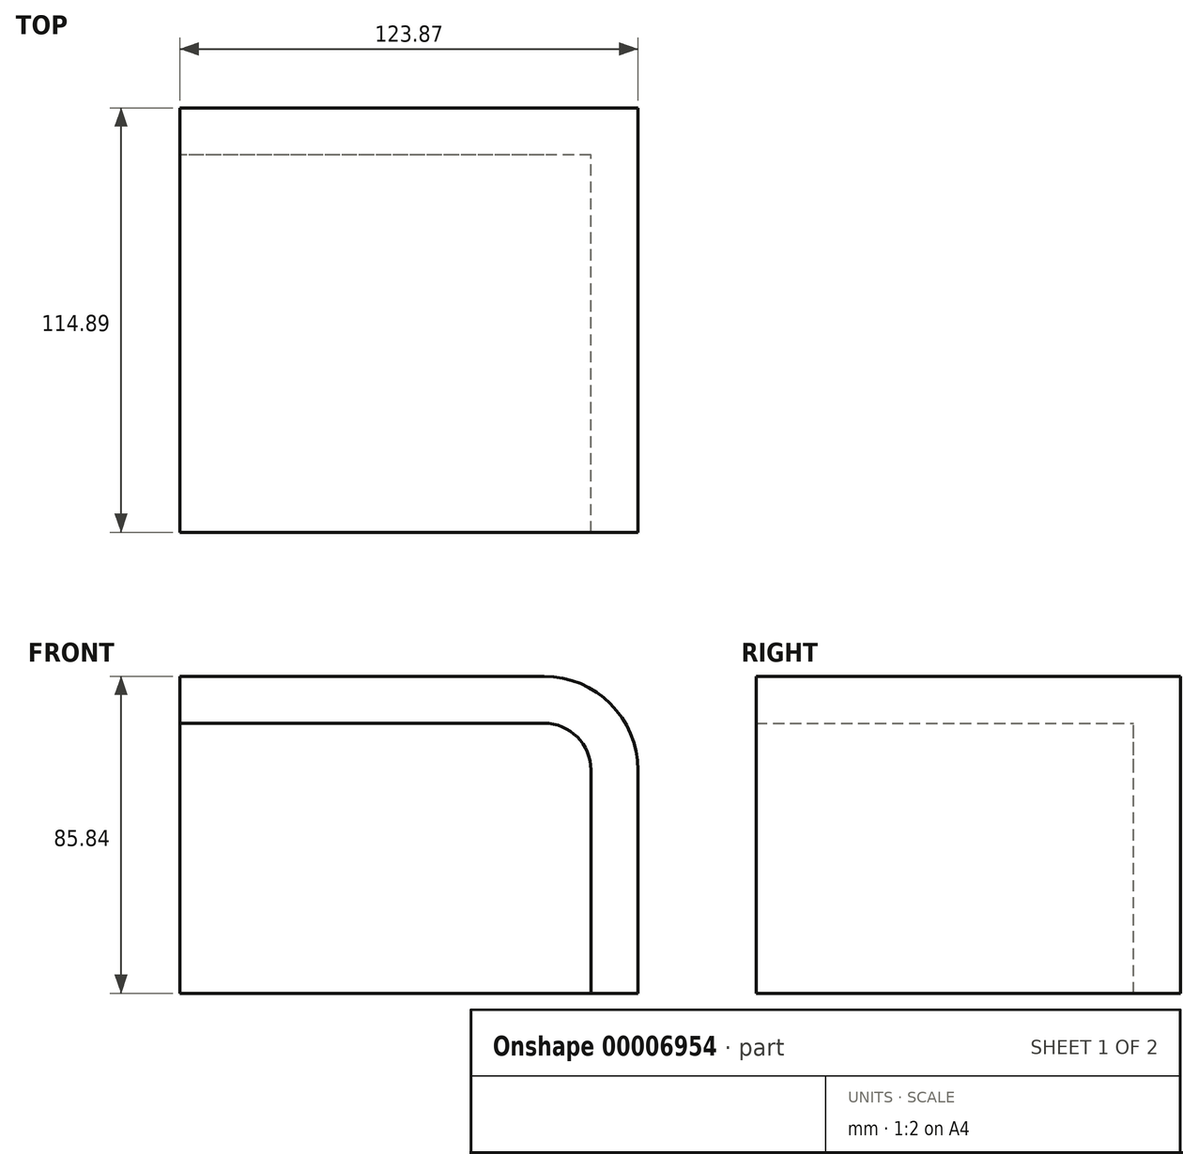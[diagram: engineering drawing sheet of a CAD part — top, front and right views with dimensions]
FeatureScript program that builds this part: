
annotation { "Feature Type Name" : "Feature", "Feature Type Description" : "" }
export const myFeature = defineFeature(function(context is Context, id is Id, definition is map)
    precondition{}
    {
        {
            var Q0;
            Q0=qCreatedBy(makeId("Right.planeOp"),FACE);
            var sketch = newSketch(context, id + "F0", { "sketchPlane" : qUnion([Q0])});
            skLineSegment(sketch, "E0.bottom", {"start": v(-56.55, -45.64) * mm, "end": v(58.34, -45.64) * mm});
            skLineSegment(sketch, "E0.top", {"start": v(-56.55, 40.2) * mm, "end": v(58.34, 40.2) * mm});
            skLineSegment(sketch, "E0.left", {"start": v(-56.55, -45.64) * mm, "end": v(-56.55, 40.2) * mm});
            skLineSegment(sketch, "E0.right", {"start": v(58.34, -45.64) * mm, "end": v(58.34, 40.2) * mm});
            skSolve(sketch);
        }
        {
            var Q0;
            Q0=makeQuery(id+"F0.imprint","IMPRINT",FACE,{"disambiguationData":[TD([[makeQuery(id+"F0.imprint","IMPRINT",EDGE,{"derivedFrom":sQuery(id+"F0.wireOp",EDGE,"E0.bottom")}),1.0]])]});
            extrude(context, id + "F1", {"entities" : qUnion([Q0]), "depth" : 123.87 * mm});
        }
        {
            var Q0;
            Q0=makeQuery(id+"F1.opExtrude","CAP_EDGE",EDGE,{"disambiguationData":[OSD([sQuery(id+"F0.wireOp",EDGE,"E0.top")])],"isStart":false});
            fillet(context, id + "F2", {"entities" : qUnion([Q0]), "radius" : 25.4 * mm, "tangentPropagation" : true, "allowEdgeOverflow" : false});
        }
        {
            var Q0;
            Q0=makeQuery(id+"F1.opExtrude","SWEPT_FACE",FACE,{"disambiguationData":[OSD([sQuery(id+"F0.wireOp",EDGE,"E0.bottom")])]});
            var Q1;
            Q1=makeQuery(id+"F1.opExtrude","SWEPT_FACE",FACE,{"disambiguationData":[OSD([sQuery(id+"F0.wireOp",EDGE,"E0.left")])]});
            var Q2;
            Q2=makeQuery(id+"F1.opExtrude","CAP_FACE",FACE,{"disambiguationData":[OSD([sQuery(id+"F0.wireOp",EDGE,"E0.bottom"),sQuery(id+"F0.wireOp",EDGE,"E0.top"),sQuery(id+"F0.wireOp",EDGE,"E0.left"),sQuery(id+"F0.wireOp",EDGE,"E0.right")])],"isStart":true});
            shell(context, id + "F3", {"entities" : qUnion([Q0, Q1, Q2]), "thickness" : 12.7 * mm});
        }
    });
